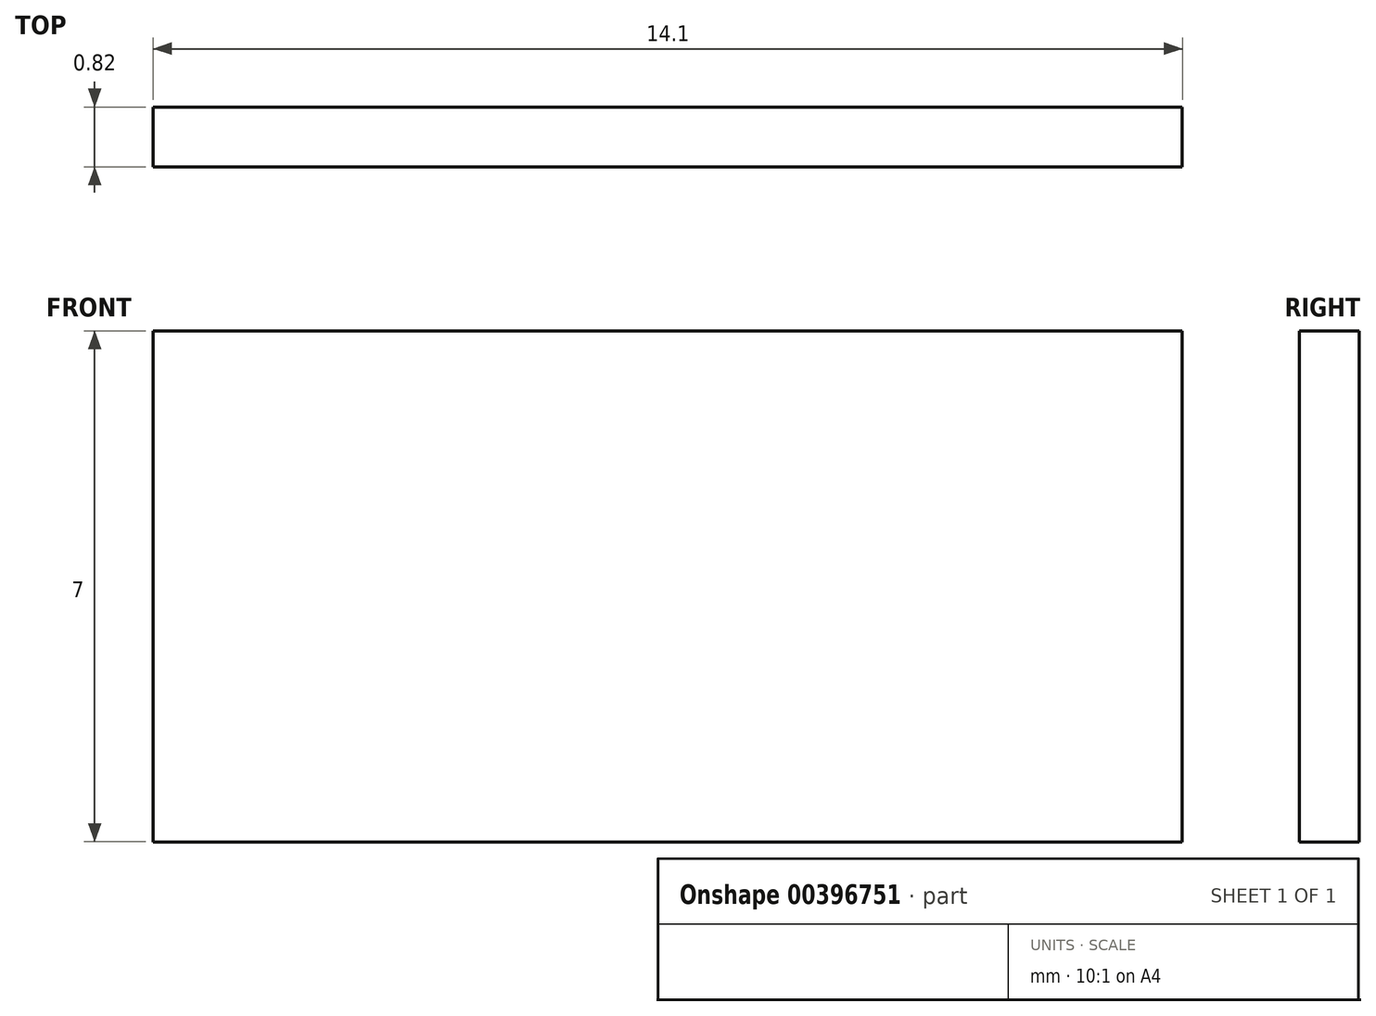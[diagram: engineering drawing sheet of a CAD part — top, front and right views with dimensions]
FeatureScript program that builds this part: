
annotation { "Feature Type Name" : "Feature", "Feature Type Description" : "" }
export const myFeature = defineFeature(function(context is Context, id is Id, definition is map)
    precondition{}
    {
        {
            var Q0;
            Q0=qCreatedBy(makeId("Front.planeOp"),FACE);
            var sketch = newSketch(context, id + "F0", { "sketchPlane" : qUnion([Q0])});
            skLineSegment(sketch, "E0.bottom", {"start": v(-11.18, 7.7) * mm, "end": v(2.92, 7.7) * mm});
            skLineSegment(sketch, "E0.top", {"start": v(-11.18, 14.7) * mm, "end": v(2.92, 14.7) * mm});
            skLineSegment(sketch, "E0.left", {"start": v(-11.18, 7.7) * mm, "end": v(-11.18, 14.7) * mm});
            skLineSegment(sketch, "E0.right", {"start": v(2.92, 7.7) * mm, "end": v(2.92, 14.7) * mm});
            skSolve(sketch);
        }
        {
            var Q0;
            Q0=makeQuery(id+"F0.imprint","IMPRINT",FACE,{"disambiguationData":[TD([[makeQuery(id+"F0.imprint","IMPRINT",EDGE,{"derivedFrom":sQuery(id+"F0.wireOp",EDGE,"E0.bottom")}),1.0]])]});
            extrude(context, id + "F1", {"entities" : qUnion([Q0]), "depth" : 0.82 * mm, "offsetDistance" : 25 * mm});
        }
    });
